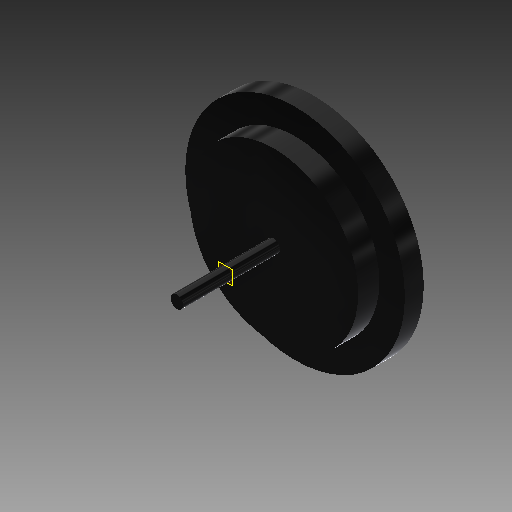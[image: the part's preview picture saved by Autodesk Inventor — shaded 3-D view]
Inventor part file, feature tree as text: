
AUTODESK INVENTOR PART (.ipt)
format: ipt  version: 2017 (Build 210142000, 142)  size: 156,672 bytes
history: native  units: in
note: dims shown in document units (in); Inventor stores cm internally (conversion verified against a paired STEP export)
features: sketch x5, other x3, plane x1
ambient origin geometry x8: Origin, YZ Plane, XZ Plane, XY Plane, X Axis, Y Axis, Z Axis, Center Point
bodies: Solid1 (feature_tree)
feature tree (9):
  other  "rueda_MIR4.ipt"
  other  "Solid1::rueda_MIR4.ipt"
  other  "TaggingFeature1"
  sketch  "Sketch2"  dims[d0=0.3937in]
  sketch  "Sketch3"
  sketch  "Sketch7"
  sketch  "Sketch12"
  sketch  "Sketch13"
  plane  "Work Plane1"
